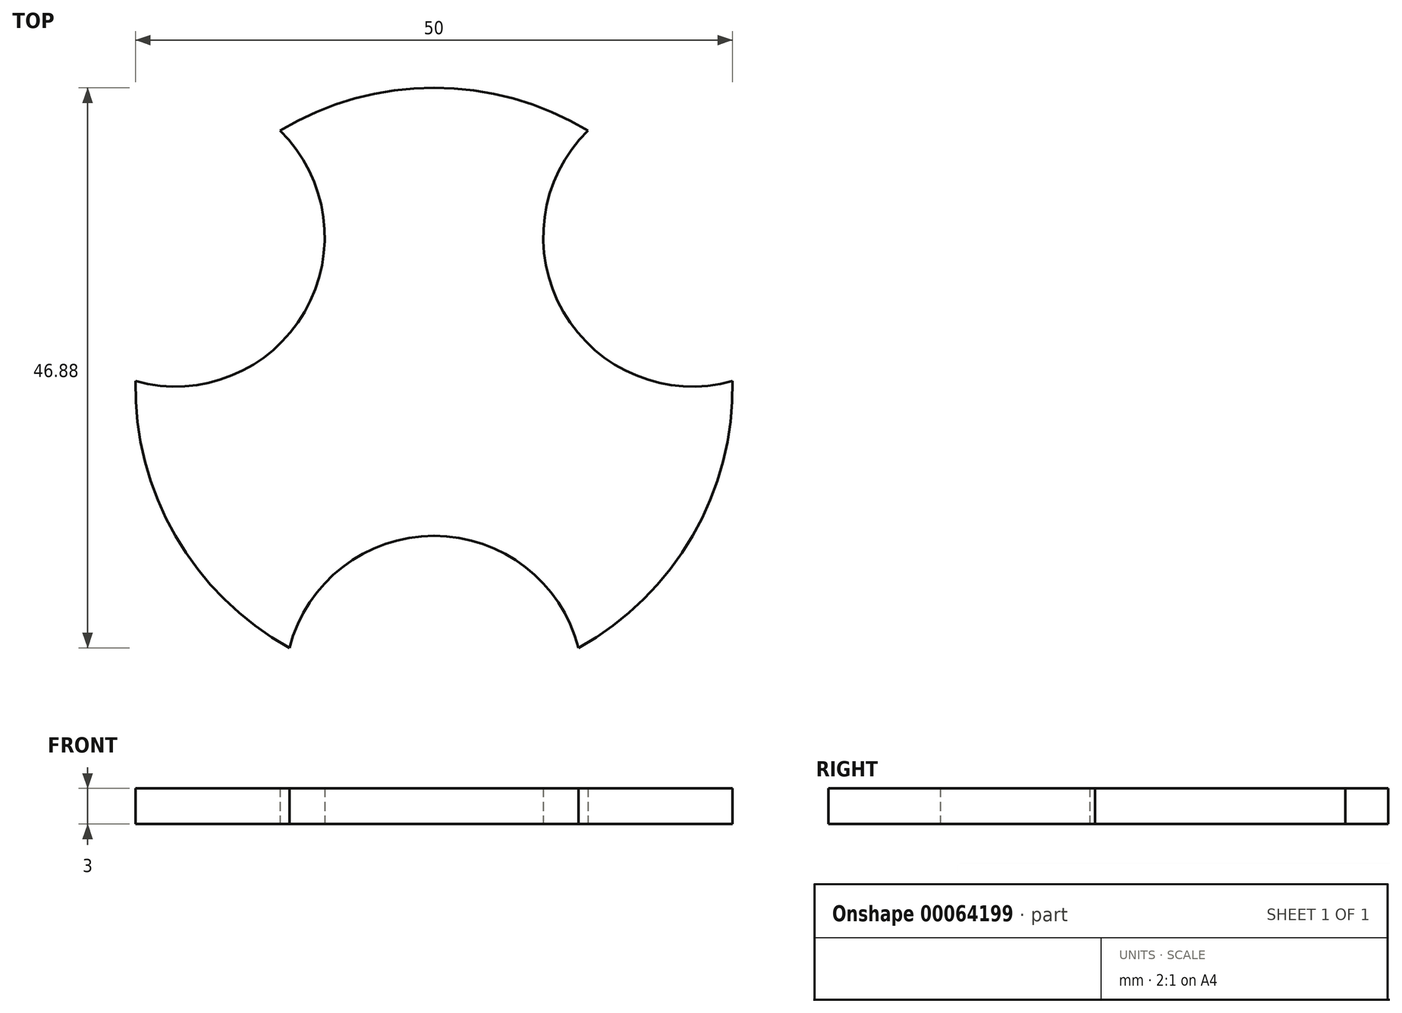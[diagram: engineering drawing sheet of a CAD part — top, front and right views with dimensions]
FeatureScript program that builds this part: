
annotation { "Feature Type Name" : "Feature", "Feature Type Description" : "" }
export const myFeature = defineFeature(function(context is Context, id is Id, definition is map)
    precondition{}
    {
        {
            var Q0;
            Q0=qCreatedBy(makeId("Top.planeOp"),FACE);
            var sketch = newSketch(context, id + "F0", { "sketchPlane" : qUnion([Q0])});
            skArc(sketch, "E0", {"start": v(-25, 0.46) * mm, "mid": v(-21.65, -12.5) * mm, "end": v(-12.1, -21.88) * mm});
            skArc(sketch, "E1", {"start": v(12.1, -21.88) * mm, "mid": v(0, -12.5) * mm, "end": v(-12.1, -21.88) * mm});
            skArc(sketch, "E2", {"start": v(-25, 0.46) * mm, "mid": v(-10.83, 6.25) * mm, "end": v(-12.9, 21.42) * mm});
            skArc(sketch, "E3", {"start": v(12.9, 21.42) * mm, "mid": v(10.83, 6.25) * mm, "end": v(25, 0.46) * mm});
            skLineSegment(sketch, "E4", {"start": v(-21.65, 12.5) * mm, "end": v(21.65, 12.5) * mm, "construction": true});
            skLineSegment(sketch, "E5", {"start": v(21.65, 12.5) * mm, "end": v(0, -25) * mm, "construction": true});
            skLineSegment(sketch, "E6", {"start": v(0, -25) * mm, "end": v(-21.65, 12.5) * mm, "construction": true});
            skArc(sketch, "E7.trimOffspring", {"start": v(12.9, 21.42) * mm, "mid": v(0, 25) * mm, "end": v(-12.9, 21.42) * mm});
            skArc(sketch, "E8.trimOffspring", {"start": v(12.1, -21.88) * mm, "mid": v(21.65, -12.5) * mm, "end": v(25, 0.46) * mm});
            skSolve(sketch);
        }
        {
            var Q0;
            Q0=makeQuery(id+"F0.imprint","IMPRINT",FACE,{"disambiguationData":[TD([[makeQuery(id+"F0.imprint","IMPRINT",EDGE,{"derivedFrom":sQuery(id+"F0.wireOp",EDGE,"E0")}),1.0]])]});
            extrude(context, id + "F1", {"entities" : qUnion([Q0]), "depth" : 3 * mm});
        }
    });
